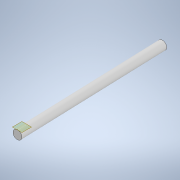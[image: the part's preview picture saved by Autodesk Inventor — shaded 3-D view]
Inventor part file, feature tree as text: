
AUTODESK INVENTOR PART (.ipt)
format: ipt  version: 2020.2 (Build 242310000, 310)  size: 105,472 bytes
history: native  units: in
note: dims shown in document units (in); Inventor stores cm internally (conversion verified against a paired STEP export)
features: other x4, extrude x2, sketch x2, plane x1
ambient origin geometry x8: Origin, YZ Plane, XZ Plane, XY Plane, X Axis, Y Axis, Z Axis, Center Point
bodies: Solid1 (feature_tree)
feature tree (9):
  plane  "Work Plane1"
  extrude  "Extrusion1"  Depth=13.5827in
  extrude  "Extrusion2"  Depth=13.5827in TaperAngle=0.0deg
  sketch  "Sketch1"  dims[d0=13.5827in d1=1.2231in]
  sketch  "Sketch2"  dims[d2=0.7874in d3=0.7874in d4=0.0in d5=13.5827in d6=0.0in]
  parser-record x1  (decoder bookkeeping rows leaked as tree rows — omitted from the tree; the rows remain in map.json)
  other  "Assembly2.iam"
  other  "Assembly3:1"
  other  "trail 9:1"
note: 1 file-system path scrubbed to <path> (originals preserved in map.json)
